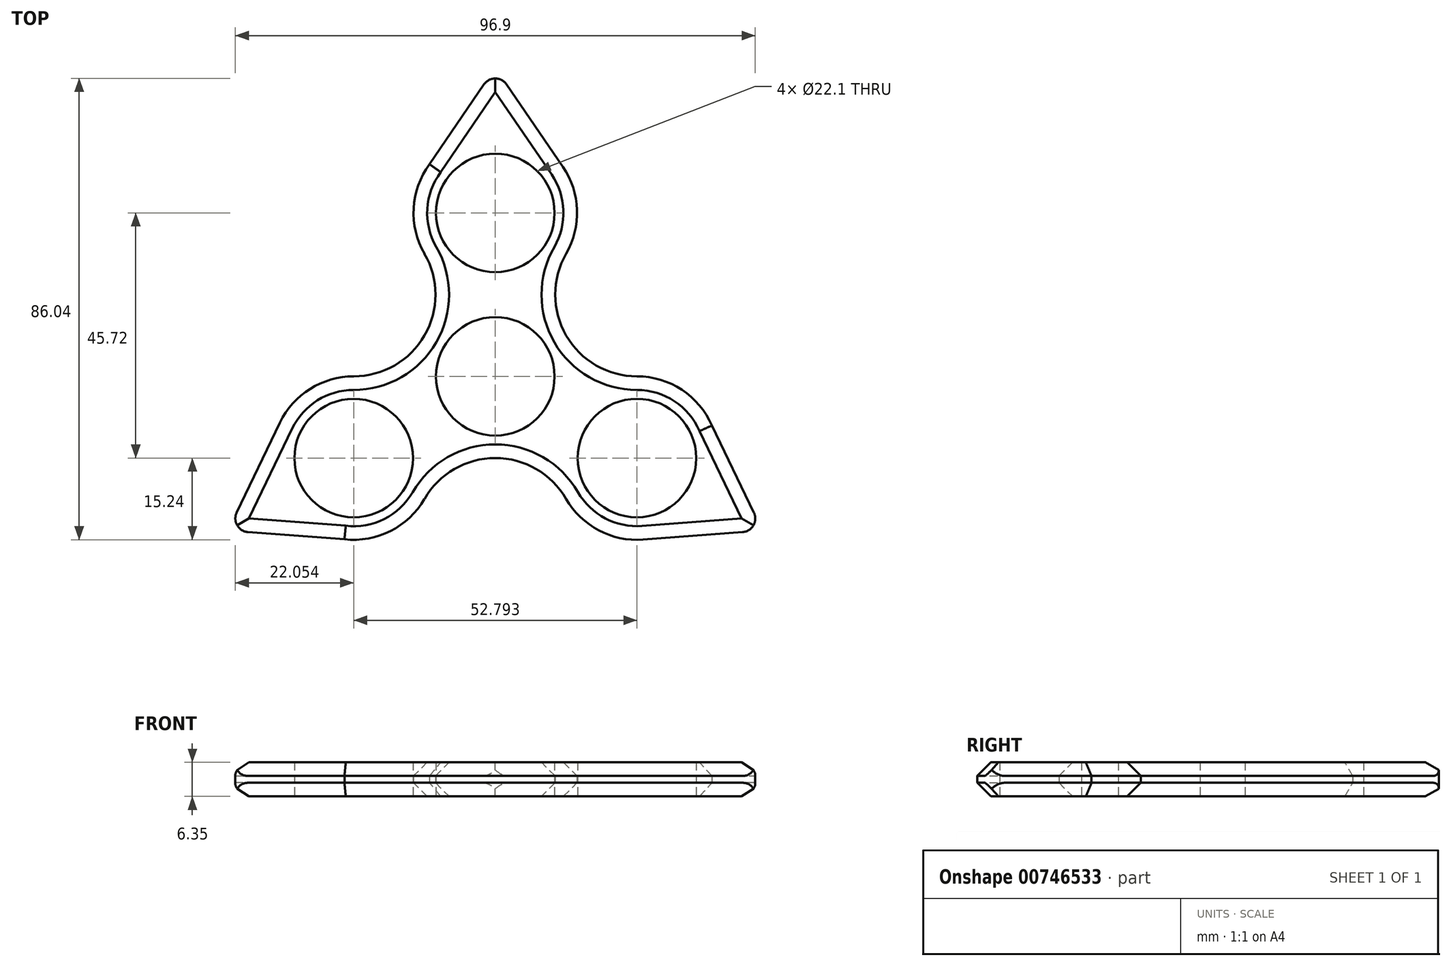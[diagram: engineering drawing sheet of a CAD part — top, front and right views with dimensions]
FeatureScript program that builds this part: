
annotation { "Feature Type Name" : "Feature", "Feature Type Description" : "" }
export const myFeature = defineFeature(function(context is Context, id is Id, definition is map)
    precondition{}
    {
        {
            var Q0;
            Q0=qCreatedBy(makeId("Top.planeOp"),FACE);
            var sketch = newSketch(context, id + "F0", { "sketchPlane" : qUnion([Q0])});
            skCircle(sketch, "E0", {"center": v(0, 0) * mm, "radius": 11.05 * mm});
            skLineSegment(sketch, "E1", {"start": v(0, 0) * mm, "end": v(0, 30.48) * mm});
            skArc(sketch, "E2", {"start": v(-12.25, 39.54) * mm, "mid": v(-15.22, 31.34) * mm, "end": v(-13.2, 22.86) * mm});
            skArc(sketch, "E3.1.0", {"start": v(-28.12, -30.38) * mm, "mid": v(-19.54, -28.85) * mm, "end": v(-13.2, -22.86) * mm});
            skArc(sketch, "E3.2.0", {"start": v(13.2, -22.86) * mm, "mid": v(19.28, -28.71) * mm, "end": v(27.54, -30.44) * mm});
            skLineSegment(sketch, "E4", {"start": v(0, 0) * mm, "end": v(-26.4, 15.24) * mm});
            skArc(sketch, "E5", {"start": v(-26.4, 0) * mm, "mid": v(-13.2, 7.62) * mm, "end": v(-13.2, 22.86) * mm});
            skArc(sketch, "E6.1.0", {"start": v(13.2, -22.86) * mm, "mid": v(0, -15.24) * mm, "end": v(-13.2, -22.86) * mm});
            skArc(sketch, "E6.2.0", {"start": v(13.2, 22.86) * mm, "mid": v(13.2, 7.62) * mm, "end": v(26.4, 0) * mm});
            skLineSegment(sketch, "E7", {"start": v(-12.25, 39.54) * mm, "end": v(0, 57.53) * mm});
            skLineSegment(sketch, "E8", {"start": v(0, 57.53) * mm, "end": v(12.6, 39.07) * mm});
            skLineSegment(sketch, "E9.1.0", {"start": v(-49.82, -28.76) * mm, "end": v(-40.13, -8.63) * mm});
            skLineSegment(sketch, "E9.2.0", {"start": v(49.82, -28.76) * mm, "end": v(27.54, -30.44) * mm});
            skLineSegment(sketch, "E10.1.0", {"start": v(-28.12, -30.38) * mm, "end": v(-49.82, -28.76) * mm});
            skLineSegment(sketch, "E10.2.0", {"start": v(40.37, -9.16) * mm, "end": v(49.82, -28.76) * mm});
            skCircle(sketch, "E11", {"center": v(0, 30.48) * mm, "radius": 11.05 * mm});
            skCircle(sketch, "E12.1.0", {"center": v(-26.4, -15.24) * mm, "radius": 11.05 * mm});
            skCircle(sketch, "E12.2.0", {"center": v(26.4, -15.24) * mm, "radius": 11.05 * mm});
            skArc(sketch, "E13.trimOffspring", {"start": v(13.2, 22.86) * mm, "mid": v(15.23, 31.05) * mm, "end": v(12.6, 39.07) * mm});
            skArc(sketch, "E14.trimOffspring", {"start": v(-26.4, 0) * mm, "mid": v(-34.5, -2.34) * mm, "end": v(-40.13, -8.63) * mm});
            skArc(sketch, "E15.trimOffspring", {"start": v(40.37, -9.16) * mm, "mid": v(34.75, -2.5) * mm, "end": v(26.4, 0) * mm});
            skSolve(sketch);
        }
        {
            var Q0;
            Q0=qSketchRegion(id+"F0",true);
            extrude(context, id + "F1", {"entities" : qUnion([Q0]), "depth" : 6.35 * mm, "offsetDistance" : 25.4 * mm});
        }
        {
            var Q0;
            Q0=makeQuery(id+"F1.opExtrude","CAP_EDGE",EDGE,{"disambiguationData":[OSD([sQuery(id+"F0.wireOp",EDGE,"E7")])],"isStart":false});
            var Q1;
            Q1=makeQuery(id+"F1.opExtrude","CAP_EDGE",EDGE,{"disambiguationData":[OSD([sQuery(id+"F0.wireOp",EDGE,"E8")])],"isStart":false});
            var Q2;
            Q2=makeQuery(id+"F1.opExtrude","CAP_EDGE",EDGE,{"disambiguationData":[OSD([sQuery(id+"F0.wireOp",EDGE,"E13.trimOffspring")])],"isStart":false});
            var Q3;
            Q3=makeQuery(id+"F1.opExtrude","CAP_EDGE",EDGE,{"disambiguationData":[OSD([sQuery(id+"F0.wireOp",EDGE,"E6.2.0")])],"isStart":false});
            var Q4;
            Q4=makeQuery(id+"F1.opExtrude","CAP_EDGE",EDGE,{"disambiguationData":[OSD([sQuery(id+"F0.wireOp",EDGE,"E15.trimOffspring")])],"isStart":false});
            var Q5;
            Q5=makeQuery(id+"F1.opExtrude","CAP_EDGE",EDGE,{"disambiguationData":[OSD([sQuery(id+"F0.wireOp",EDGE,"E10.2.0")])],"isStart":false});
            var Q6;
            Q6=makeQuery(id+"F1.opExtrude","CAP_EDGE",EDGE,{"disambiguationData":[OSD([sQuery(id+"F0.wireOp",EDGE,"E9.2.0")])],"isStart":false});
            var Q7;
            Q7=makeQuery(id+"F1.opExtrude","CAP_EDGE",EDGE,{"disambiguationData":[OSD([sQuery(id+"F0.wireOp",EDGE,"E2")])],"isStart":false});
            var Q8;
            Q8=makeQuery(id+"F1.opExtrude","CAP_EDGE",EDGE,{"disambiguationData":[OSD([sQuery(id+"F0.wireOp",EDGE,"E5")])],"isStart":false});
            var Q9;
            Q9=makeQuery(id+"F1.opExtrude","CAP_EDGE",EDGE,{"disambiguationData":[OSD([sQuery(id+"F0.wireOp",EDGE,"E14.trimOffspring")])],"isStart":false});
            var Q10;
            Q10=makeQuery(id+"F1.opExtrude","CAP_EDGE",EDGE,{"disambiguationData":[OSD([sQuery(id+"F0.wireOp",EDGE,"E9.1.0")])],"isStart":false});
            var Q11;
            Q11=makeQuery(id+"F1.opExtrude","CAP_EDGE",EDGE,{"disambiguationData":[OSD([sQuery(id+"F0.wireOp",EDGE,"E10.1.0")])],"isStart":false});
            var Q12;
            Q12=makeQuery(id+"F1.opExtrude","CAP_EDGE",EDGE,{"disambiguationData":[OSD([sQuery(id+"F0.wireOp",EDGE,"E3.1.0")])],"isStart":false});
            var Q13;
            Q13=makeQuery(id+"F1.opExtrude","CAP_EDGE",EDGE,{"disambiguationData":[OSD([sQuery(id+"F0.wireOp",EDGE,"E6.1.0")])],"isStart":false});
            var Q14;
            Q14=makeQuery(id+"F1.opExtrude","CAP_EDGE",EDGE,{"disambiguationData":[OSD([sQuery(id+"F0.wireOp",EDGE,"E3.2.0")])],"isStart":false});
            chamfer(context, id + "F2", {"entities" : qUnion([Q0, Q1, Q2, Q3, Q4, Q5, Q6, Q7, Q8, Q9, Q10, Q11, Q12, Q13, Q14]), "width" : 2.54 * mm, "tangentPropagation" : true});
        }
        {
            var Q0;
            Q0=makeQuery(id+"F1.opExtrude","CAP_EDGE",EDGE,{"disambiguationData":[OSD([sQuery(id+"F0.wireOp",EDGE,"E8")])],"isStart":true});
            var Q1;
            Q1=makeQuery(id+"F1.opExtrude","CAP_EDGE",EDGE,{"disambiguationData":[OSD([sQuery(id+"F0.wireOp",EDGE,"E7")])],"isStart":true});
            var Q2;
            Q2=makeQuery(id+"F1.opExtrude","CAP_EDGE",EDGE,{"disambiguationData":[OSD([sQuery(id+"F0.wireOp",EDGE,"E2")])],"isStart":true});
            var Q3;
            Q3=makeQuery(id+"F1.opExtrude","CAP_EDGE",EDGE,{"disambiguationData":[OSD([sQuery(id+"F0.wireOp",EDGE,"E10.1.0")])],"isStart":true});
            var Q4;
            Q4=makeQuery(id+"F1.opExtrude","CAP_EDGE",EDGE,{"disambiguationData":[OSD([sQuery(id+"F0.wireOp",EDGE,"E3.1.0")])],"isStart":true});
            var Q5;
            Q5=makeQuery(id+"F1.opExtrude","CAP_EDGE",EDGE,{"disambiguationData":[OSD([sQuery(id+"F0.wireOp",EDGE,"E6.1.0")])],"isStart":true});
            var Q6;
            Q6=makeQuery(id+"F1.opExtrude","CAP_EDGE",EDGE,{"disambiguationData":[OSD([sQuery(id+"F0.wireOp",EDGE,"E3.2.0")])],"isStart":true});
            var Q7;
            Q7=makeQuery(id+"F1.opExtrude","CAP_EDGE",EDGE,{"disambiguationData":[OSD([sQuery(id+"F0.wireOp",EDGE,"E9.2.0")])],"isStart":true});
            var Q8;
            Q8=makeQuery(id+"F1.opExtrude","CAP_EDGE",EDGE,{"disambiguationData":[OSD([sQuery(id+"F0.wireOp",EDGE,"E10.2.0")])],"isStart":true});
            var Q9;
            Q9=makeQuery(id+"F1.opExtrude","CAP_EDGE",EDGE,{"disambiguationData":[OSD([sQuery(id+"F0.wireOp",EDGE,"E15.trimOffspring")])],"isStart":true});
            var Q10;
            Q10=makeQuery(id+"F1.opExtrude","CAP_EDGE",EDGE,{"disambiguationData":[OSD([sQuery(id+"F0.wireOp",EDGE,"E6.2.0")])],"isStart":true});
            var Q11;
            Q11=makeQuery(id+"F1.opExtrude","CAP_EDGE",EDGE,{"disambiguationData":[OSD([sQuery(id+"F0.wireOp",EDGE,"E13.trimOffspring")])],"isStart":true});
            var Q12;
            Q12=makeQuery(id+"F1.opExtrude","CAP_EDGE",EDGE,{"disambiguationData":[OSD([sQuery(id+"F0.wireOp",EDGE,"E5")])],"isStart":true});
            var Q13;
            Q13=makeQuery(id+"F1.opExtrude","CAP_EDGE",EDGE,{"disambiguationData":[OSD([sQuery(id+"F0.wireOp",EDGE,"E14.trimOffspring")])],"isStart":true});
            var Q14;
            Q14=makeQuery(id+"F1.opExtrude","CAP_EDGE",EDGE,{"disambiguationData":[OSD([sQuery(id+"F0.wireOp",EDGE,"E9.1.0")])],"isStart":true});
            chamfer(context, id + "F3", {"entities" : qUnion([Q0, Q1, Q2, Q3, Q4, Q5, Q6, Q7, Q8, Q9, Q10, Q11, Q12, Q13, Q14]), "width" : 2.54 * mm, "tangentPropagation" : true});
        }
        {
            var Q0;
            Q0=makeQuery(id+"F1.opExtrude","SWEPT_EDGE",EDGE,{"disambiguationData":[OSD([sQuery(id+"F0.wireOp",EDGE,"E9.1.0"),sQuery(id+"F0.wireOp",EDGE,"E10.1.0")])]});
            var Q1;
            Q1=makeQuery(id+"F1.opExtrude","SWEPT_EDGE",EDGE,{"disambiguationData":[OSD([sQuery(id+"F0.wireOp",EDGE,"E7"),sQuery(id+"F0.wireOp",EDGE,"E8")])]});
            fillet(context, id + "F4", {"entities" : qUnion([Q0, Q1]), "radius" : 2.54 * mm, "tangentPropagation" : true, "allowEdgeOverflow" : false});
        }
        {
            var Q0;
            Q0=makeQuery(id+"F1.opExtrude","SWEPT_EDGE",EDGE,{"disambiguationData":[OSD([sQuery(id+"F0.wireOp",EDGE,"E9.2.0"),sQuery(id+"F0.wireOp",EDGE,"E10.2.0")])]});
            fillet(context, id + "F5", {"entities" : qUnion([Q0]), "radius" : 2.54 * mm, "tangentPropagation" : true, "allowEdgeOverflow" : false});
        }
    });
